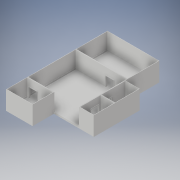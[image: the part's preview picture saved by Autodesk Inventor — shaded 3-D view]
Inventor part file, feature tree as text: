
AUTODESK INVENTOR PART (.ipt)
format: ipt  version: 2017 (Build 210142000, 142)  size: 407,552 bytes
history: native  units: in
note: dims shown in document units (in); Inventor stores cm internally (conversion verified against a paired STEP export)
features: extrude x9, sketch x7, other x2, plane x1
ambient origin geometry x8: Origin, YZ Plane, XZ Plane, XY Plane, X Axis, Y Axis, Z Axis, Center Point
bodies: Solid1 (feature_tree)
feature tree (19):
  extrude  "floor"  Depth=30.5in
  extrude  "walls"  Depth=15.5in
  extrude  "trim"  Depth=11.5in
  extrude  "doorframe 1 and 2"  Depth=14.5in
  extrude  "door frame 3"  Depth=39.0in
  extrude  "door frame 4"  Depth=1.0in TaperAngle=0.0deg
  other  "door trim workplane 1 and 2"
  extrude  "door trim 1 and 2"  Depth=0.25in
  other  "door time workplane 3"
  extrude  "door trim 3"  Depth=0.25in
  plane  "Work Plane3"
  extrude  "door trim 4"  Depth=0.25in
  sketch  "Sketch1"  dims[d0=35.5in d1=30.5in]
  sketch  "Sketch4"  dims[d2=12.5in d3=15.5in]
  sketch  "Sketch5"  dims[d4=12.5in d5=11.5in]
  sketch  "Sketch7"  dims[d6=12.5in d7=14.5in]
  sketch  "Sketch8"  dims[d9=18.5in d11=39.0in]
  sketch  "Sketch9"  dims[d12=30.5in d13=1.0in d14=0.0in]
  sketch  "Sketch10"  dims[d27=12.5in d28=0.25in d30=0.25in d31=0.25in d34=0.25in d38=0.25in d39=0.25in d40=0.25in d41=0.25in d42=0.25in d43=0.25in d44=10.0in d45=0.0in d48=0.25in d49=0.25in d50=0.25in d51=0.25in d52=0.0833in d55=0.0833in d56=0.0833in d57=0.828in d58=0.0in d59=4.8613in d60=5.7039in d61=1.0in d63=0.5in d64=0.25in d67=38.75in d68=0.0in d69=26.75in d70=0.0833in d71=0.0833in d76=0.0833in d77=0.0833in d78=0.0833in d79=0.0833in d80=0.0833in d81=0.828in d82=0.0in d83=4.8613in d84=5.7039in d86=10.0in d87=0.828in d88=0.0in d89=4.8613in d90=5.7039in d91=1.0in d92=0.828in d93=0.0in d94=0.305in d95=0.305in d96=0.305in d97=0.305in d98=0.305in d99=0.305in d100=1.0in d101=0.0in d102=0.305in d103=0.305in d104=0.305in d105=0.305in d106=1.0in d107=0.0in d108=0.305in d109=0.305in d110=0.305in d111=0.305in d112=1.0in d113=0.0in d114=0.25in]
